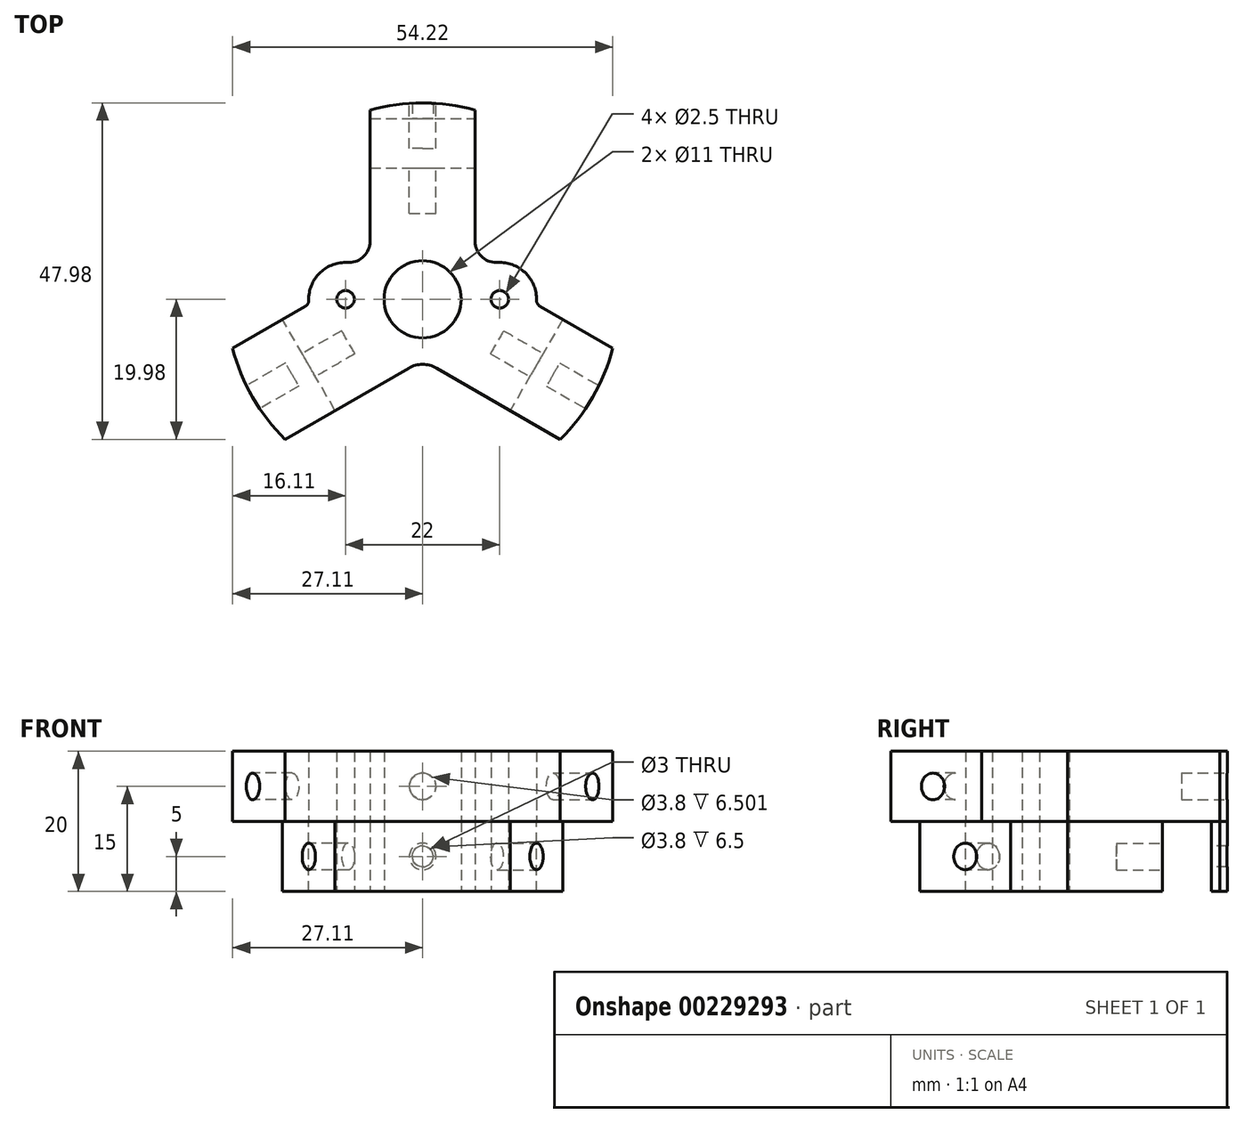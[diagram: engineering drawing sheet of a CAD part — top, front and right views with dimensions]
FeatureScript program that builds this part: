
annotation { "Feature Type Name" : "Feature", "Feature Type Description" : "" }
export const myFeature = defineFeature(function(context is Context, id is Id, definition is map)
    precondition{}
    {
        {
            var Q0;
            Q0=qCreatedBy(makeId("Top.planeOp"),FACE);
            var sketch = newSketch(context, id + "F0", { "sketchPlane" : qUnion([Q0])});
            skArc(sketch, "E0", {"start": v(7.5, 26.98) * mm, "mid": v(0, 28) * mm, "end": v(-7.5, 26.98) * mm});
            skCircle(sketch, "E1", {"center": v(0, 0) * mm, "radius": 5.5 * mm});
            skCircle(sketch, "E2", {"center": v(-11, 0) * mm, "radius": 1.25 * mm});
            skCircle(sketch, "E3", {"center": v(11, 0) * mm, "radius": 1.25 * mm});
            skArc(sketch, "E4", {"start": v(-7.5, 17.18) * mm, "mid": v(-16.24, 9.37) * mm, "end": v(-18.63, -2.1) * mm});
            skCircle(sketch, "E5", {"center": v(0, 0) * mm, "radius": 25.75 * mm, "construction": true});
            skLineSegment(sketch, "E6", {"start": v(12.25, 0) * mm, "end": v(18.75, 0) * mm, "construction": true});
            skLineSegment(sketch, "E7", {"start": v(-7.5, 18.75) * mm, "end": v(7.5, 18.75) * mm});
            skLineSegment(sketch, "E8", {"start": v(-7.5, 18.75) * mm, "end": v(-7.5, 17.18) * mm});
            skLineSegment(sketch, "E9", {"start": v(7.5, 18.75) * mm, "end": v(7.5, 17.18) * mm});
            skLineSegment(sketch, "E10", {"start": v(-7.5, 25.75) * mm, "end": v(7.5, 25.75) * mm});
            skLineSegment(sketch, "E11", {"start": v(-7.5, 25.75) * mm, "end": v(-7.5, 26.98) * mm});
            skLineSegment(sketch, "E12", {"start": v(7.5, 25.75) * mm, "end": v(7.5, 26.98) * mm});
            skLineSegment(sketch, "E13.1.0", {"start": v(-12.49, -15.87) * mm, "end": v(-19.99, -2.88) * mm});
            skLineSegment(sketch, "E13.1.3", {"start": v(-19.99, -2.88) * mm, "end": v(-18.63, -2.1) * mm});
            skLineSegment(sketch, "E13.1.6", {"start": v(-12.49, -15.87) * mm, "end": v(-11.13, -15.09) * mm});
            skLineSegment(sketch, "E13.2.0", {"start": v(19.99, -2.88) * mm, "end": v(12.49, -15.87) * mm});
            skLineSegment(sketch, "E13.2.3", {"start": v(12.49, -15.87) * mm, "end": v(11.13, -15.09) * mm});
            skLineSegment(sketch, "E13.2.6", {"start": v(19.99, -2.88) * mm, "end": v(18.63, -2.1) * mm});
            skArc(sketch, "E14.trimOffspring", {"start": v(-11.13, -15.09) * mm, "mid": v(0, -18.75) * mm, "end": v(11.13, -15.09) * mm});
            skArc(sketch, "E15.trimOffspring", {"start": v(18.63, -2.1) * mm, "mid": v(16.24, 9.37) * mm, "end": v(7.5, 17.18) * mm});
            skSolve(sketch);
        }
        {
            var Q0;
            Q0 = qSketchRegion(id + "F0", true);
            extrude(context, id + "F1", {"entities" : qUnion([Q0]), "depth" : 10 * mm});
        }
        {
            var Q0;
            Q0=makeQuery(id+"F1.opExtrude","SWEPT_FACE",FACE,{"disambiguationData":[OSD([sQuery(id+"F0.wireOp",EDGE,"E13.1.0")])]});
            var sketch = newSketch(context, id + "F2", { "sketchPlane" : qUnion([Q0])});
            skLineSegment(sketch, "E16", {"start": v(0, 10) * mm, "end": v(0, 0) * mm, "construction": true});
            skCircle(sketch, "E17", {"center": v(0, 5) * mm, "radius": 1.9 * mm});
            skSolve(sketch);
        }
        {
            var Q0;
            Q0 = qSketchRegion(id + "F2", true);
            extrude(context, id + "F3", {"entities" : qUnion([Q0]), "oppositeDirection" : true, "depth" : 6.5 * mm});
        }
        {
            var Q0;
            Q0=makeQuery(id+"F3.opExtrude","SWEPT_BODY",BODY,{"disambiguationData":[OSD([sQuery(id+"F2.wireOp",EDGE,"E17")])]});
            var Q1;
            Q1=makeQuery(id+"F1.opExtrude","SWEPT_FACE",FACE,{"disambiguationData":[OSD([sQuery(id+"F0.wireOp",EDGE,"E1")])]});
            circularPattern(context, id + "F4", {"entities" : qUnion([Q0]), "axis" : qUnion([Q1]), "angle" : 360 * degree, "instanceCount" : 3, "equalSpace" : true});
        }
        {
            var Q0;
            Q0=makeQuery(id+"F3.opExtrude","SWEPT_BODY",BODY,{"disambiguationData":[OSD([sQuery(id+"F2.wireOp",EDGE,"E17")])]});
            var Q1;
            Q1=makeQuery(id+"F4.opPattern","COPY",BODY,{"derivedFrom":makeQuery(id+"F3.opExtrude","SWEPT_BODY",BODY,{"disambiguationData":[OSD([sQuery(id+"F2.wireOp",EDGE,"E17")])]}),"instanceName":"1"});
            var Q2;
            Q2=makeQuery(id+"F4.opPattern","COPY",BODY,{"derivedFrom":makeQuery(id+"F3.opExtrude","SWEPT_BODY",BODY,{"disambiguationData":[OSD([sQuery(id+"F2.wireOp",EDGE,"E17")])]}),"instanceName":"2"});
            var Q3;
            Q3=makeQuery(id+"F1.opExtrude","SWEPT_BODY",BODY,{"disambiguationData":[OSD([sQuery(id+"F0.wireOp",EDGE,"E1"),sQuery(id+"F0.wireOp",EDGE,"E2"),sQuery(id+"F0.wireOp",EDGE,"E3"),sQuery(id+"F0.wireOp",EDGE,"E4"),sQuery(id+"F0.wireOp",EDGE,"E7"),sQuery(id+"F0.wireOp",EDGE,"E8"),sQuery(id+"F0.wireOp",EDGE,"E9"),sQuery(id+"F0.wireOp",EDGE,"E13.1.0"),sQuery(id+"F0.wireOp",EDGE,"E13.1.3"),sQuery(id+"F0.wireOp",EDGE,"E13.1.6"),sQuery(id+"F0.wireOp",EDGE,"E13.2.0"),sQuery(id+"F0.wireOp",EDGE,"E13.2.3"),sQuery(id+"F0.wireOp",EDGE,"E13.2.6"),sQuery(id+"F0.wireOp",EDGE,"E14.trimOffspring"),sQuery(id+"F0.wireOp",EDGE,"E15.trimOffspring")])]});
            booleanBodies(context, id + "F5", {"operationType" : BooleanOperationType.SUBTRACTION, "tools" : qUnion([Q0, Q1, Q2]), "targets" : qUnion([Q3])});
        }
        {
            var Q0;
            Q0=makeQuery(id+"F1.opExtrude","SWEPT_FACE",FACE,{"disambiguationData":[OSD([sQuery(id+"F0.wireOp",EDGE,"E10")])]});
            var sketch = newSketch(context, id + "F6", { "sketchPlane" : qUnion([Q0])});
            skLineSegment(sketch, "E18", {"start": v(0, 10) * mm, "end": v(0, 0) * mm, "construction": true});
            skCircle(sketch, "E19", {"center": v(0, 5) * mm, "radius": 1.5 * mm});
            skSolve(sketch);
        }
        {
            var Q0;
            Q0 = qSketchRegion(id + "F6", true);
            var Q1;
            Q1=sQuery(id+"F6.wireOp",EDGE,"E19");
            extrude(context, id + "F7", {"entities" : qUnion([Q0]), "operationType" : NewBodyOperationType.REMOVE, "surfaceEntities" : qUnion([Q1]), "endBound" : BoundingType.UP_TO_NEXT, "oppositeDirection" : true, "depth" : 25 * mm});
        }
        {
            var Q0;
            Q0=makeQuery(id+"F1.opExtrude","CAP_FACE",FACE,{"disambiguationData":[OSD([sQuery(id+"F0.wireOp",EDGE,"E1"),sQuery(id+"F0.wireOp",EDGE,"E2"),sQuery(id+"F0.wireOp",EDGE,"E3"),sQuery(id+"F0.wireOp",EDGE,"E4"),sQuery(id+"F0.wireOp",EDGE,"E7"),sQuery(id+"F0.wireOp",EDGE,"E8"),sQuery(id+"F0.wireOp",EDGE,"E9"),sQuery(id+"F0.wireOp",EDGE,"E13.1.0"),sQuery(id+"F0.wireOp",EDGE,"E13.1.3"),sQuery(id+"F0.wireOp",EDGE,"E13.1.6"),sQuery(id+"F0.wireOp",EDGE,"E13.2.0"),sQuery(id+"F0.wireOp",EDGE,"E13.2.3"),sQuery(id+"F0.wireOp",EDGE,"E13.2.6"),sQuery(id+"F0.wireOp",EDGE,"E14.trimOffspring"),sQuery(id+"F0.wireOp",EDGE,"E15.trimOffspring")])],"isStart":false});
            var sketch = newSketch(context, id + "F8", { "sketchPlane" : qUnion([Q0])});
            skArc(sketch, "E20", {"start": v(-11, 5.25) * mm, "mid": v(-14.75, 3.67) * mm, "end": v(-16.25, -0.12) * mm});
            skArc(sketch, "E21", {"start": v(16.25, -0.12) * mm, "mid": v(14.75, 3.67) * mm, "end": v(11, 5.25) * mm});
            skLineSegment(sketch, "E22", {"start": v(-11, 5.25) * mm, "end": v(-10.5, 5.25) * mm});
            skLineSegment(sketch, "E23", {"start": v(-7.5, 17.18) * mm, "end": v(-7.5, 8.25) * mm});
            skLineSegment(sketch, "E24", {"start": v(7.5, 17.18) * mm, "end": v(7.5, 8.25) * mm});
            skLineSegment(sketch, "E25", {"start": v(-18.63, -2.1) * mm, "end": v(-16.75, -1) * mm});
            skLineSegment(sketch, "E26", {"start": v(18.63, -2.1) * mm, "end": v(16.75, -1) * mm});
            skLineSegment(sketch, "E27.trimOffspring", {"start": v(10.5, 5.25) * mm, "end": v(11, 5.25) * mm});
            skPoint(sketch, "E28.visualSharp", {"position": v(-7.5, 5.25) * mm});
            skArc(sketch, "E28.filletArc", {"start": v(-10.5, 5.25) * mm, "mid": v(-8.38, 6.13) * mm, "end": v(-7.5, 8.25) * mm});
            skPoint(sketch, "E29.visualSharp", {"position": v(7.5, 5.25) * mm});
            skArc(sketch, "E29.filletArc", {"start": v(7.5, 8.25) * mm, "mid": v(8.38, 6.13) * mm, "end": v(10.5, 5.25) * mm});
            skPoint(sketch, "E30.visualSharp", {"position": v(-16.2, -0.7) * mm});
            skArc(sketch, "E30.filletArc", {"start": v(-16.75, -1) * mm, "mid": v(-16.38, -0.63) * mm, "end": v(-16.25, -0.12) * mm});
            skPoint(sketch, "E31.visualSharp", {"position": v(16.2, -0.7) * mm});
            skArc(sketch, "E31.filletArc", {"start": v(16.25, -0.12) * mm, "mid": v(16.38, -0.63) * mm, "end": v(16.75, -1) * mm});
            skArc(sketch, "E32", {"start": v(18.63, -2.1) * mm, "mid": v(16.24, 9.38) * mm, "end": v(7.5, 17.18) * mm});
            skArc(sketch, "E33", {"start": v(-7.5, 17.18) * mm, "mid": v(-16.24, 9.37) * mm, "end": v(-18.63, -2.1) * mm});
            skLineSegment(sketch, "E34", {"start": v(-11.13, -15.09) * mm, "end": v(-2, -9.81) * mm});
            skLineSegment(sketch, "E35", {"start": v(2, -9.81) * mm, "end": v(11.13, -15.09) * mm});
            skPoint(sketch, "E36.visualSharp", {"position": v(0, -8.66) * mm});
            skArc(sketch, "E36.filletArc", {"start": v(2, -9.81) * mm, "mid": v(0, -9.28) * mm, "end": v(-2, -9.81) * mm});
            skArc(sketch, "E37", {"start": v(-11.13, -15.09) * mm, "mid": v(0, -18.75) * mm, "end": v(11.13, -15.09) * mm});
            skSolve(sketch);
        }
        {
            var Q0;
            Q0 = qSketchRegion(id + "F8", true);
            extrude(context, id + "F9", {"entities" : qUnion([Q0]), "operationType" : NewBodyOperationType.REMOVE, "endBound" : BoundingType.UP_TO_NEXT, "oppositeDirection" : true, "depth" : 25 * mm});
        }
        {
            var Q0;
            Q0=makeQuery(id+"F1.opExtrude","CAP_FACE",FACE,{"disambiguationData":[OSD([sQuery(id+"F0.wireOp",EDGE,"E1"),sQuery(id+"F0.wireOp",EDGE,"E2"),sQuery(id+"F0.wireOp",EDGE,"E3"),sQuery(id+"F0.wireOp",EDGE,"E4"),sQuery(id+"F0.wireOp",EDGE,"E7"),sQuery(id+"F0.wireOp",EDGE,"E8"),sQuery(id+"F0.wireOp",EDGE,"E9"),sQuery(id+"F0.wireOp",EDGE,"E13.1.0"),sQuery(id+"F0.wireOp",EDGE,"E13.1.3"),sQuery(id+"F0.wireOp",EDGE,"E13.1.6"),sQuery(id+"F0.wireOp",EDGE,"E13.2.0"),sQuery(id+"F0.wireOp",EDGE,"E13.2.3"),sQuery(id+"F0.wireOp",EDGE,"E13.2.6"),sQuery(id+"F0.wireOp",EDGE,"E14.trimOffspring"),sQuery(id+"F0.wireOp",EDGE,"E15.trimOffspring")])],"isStart":false});
            var sketch = newSketch(context, id + "F10", { "sketchPlane" : qUnion([Q0])});
            skArc(sketch, "E38", {"start": v(-27.11, -7) * mm, "mid": v(-24.25, -14) * mm, "end": v(-19.61, -19.98) * mm});
            skCircle(sketch, "E39", {"center": v(0, 0) * mm, "radius": 5.5 * mm});
            skCircle(sketch, "E40", {"center": v(-11, 0) * mm, "radius": 1.25 * mm});
            skCircle(sketch, "E41", {"center": v(11, 0) * mm, "radius": 1.25 * mm});
            skArc(sketch, "E42", {"start": v(-11, 5.25) * mm, "mid": v(-14.75, 3.67) * mm, "end": v(-16.25, -0.12) * mm});
            skArc(sketch, "E43", {"start": v(16.25, -0.12) * mm, "mid": v(14.75, 3.67) * mm, "end": v(11, 5.25) * mm});
            skLineSegment(sketch, "E44", {"start": v(-11, 5.25) * mm, "end": v(-10.5, 5.25) * mm});
            skLineSegment(sketch, "E45", {"start": v(-7.5, 26.98) * mm, "end": v(-7.5, 8.25) * mm});
            skLineSegment(sketch, "E46", {"start": v(7.5, 26.98) * mm, "end": v(7.5, 8.25) * mm});
            skLineSegment(sketch, "E47", {"start": v(27.11, -7) * mm, "end": v(16.75, -1) * mm});
            skLineSegment(sketch, "E48", {"start": v(19.61, -19.98) * mm, "end": v(2, -9.81) * mm});
            skLineSegment(sketch, "E49", {"start": v(-2, -9.81) * mm, "end": v(-19.61, -19.98) * mm});
            skLineSegment(sketch, "E50", {"start": v(-27.11, -7) * mm, "end": v(-16.75, -1) * mm});
            skArc(sketch, "E51.trimOffspring", {"start": v(7.5, 26.98) * mm, "mid": v(0, 28) * mm, "end": v(-7.5, 26.98) * mm});
            skArc(sketch, "E52.trimOffspring", {"start": v(19.61, -19.98) * mm, "mid": v(24.25, -14) * mm, "end": v(27.11, -7) * mm});
            skLineSegment(sketch, "E53.trimOffspring", {"start": v(10.5, 5.25) * mm, "end": v(11, 5.25) * mm});
            skPoint(sketch, "E54.visualSharp", {"position": v(0, -8.66) * mm});
            skArc(sketch, "E54.filletArc", {"start": v(2, -9.81) * mm, "mid": v(0, -9.28) * mm, "end": v(-2, -9.81) * mm});
            skPoint(sketch, "E55.visualSharp", {"position": v(-7.5, 5.25) * mm});
            skArc(sketch, "E55.filletArc", {"start": v(-10.5, 5.25) * mm, "mid": v(-8.38, 6.13) * mm, "end": v(-7.5, 8.25) * mm});
            skPoint(sketch, "E56.visualSharp", {"position": v(7.5, 5.25) * mm});
            skArc(sketch, "E56.filletArc", {"start": v(7.5, 8.25) * mm, "mid": v(8.38, 6.13) * mm, "end": v(10.5, 5.25) * mm});
            skPoint(sketch, "E57.visualSharp", {"position": v(16.2, -0.7) * mm});
            skArc(sketch, "E57.filletArc", {"start": v(16.25, -0.12) * mm, "mid": v(16.38, -0.63) * mm, "end": v(16.75, -1) * mm});
            skPoint(sketch, "E58.visualSharp", {"position": v(-16.2, -0.7) * mm});
            skArc(sketch, "E58.filletArc", {"start": v(-16.75, -1) * mm, "mid": v(-16.38, -0.63) * mm, "end": v(-16.25, -0.12) * mm});
            skSolve(sketch);
        }
        {
            var Q0;
            Q0 = qSketchRegion(id + "F10", true);
            extrude(context, id + "F11", {"entities" : qUnion([Q0]), "depth" : 10 * mm});
        }
        {
            var Q0;
            Q0=makeQuery(id+"F11.opExtrude","CAP_EDGE",EDGE,{"disambiguationData":[OSD([sQuery(id+"F10.wireOp",EDGE,"E51.trimOffspring")])],"isStart":false});
            cPoint(context, id + "F12", {"entities" : qUnion([Q0]), "parameter" : 0.5});
        }
        {
            var Q0;
            Q0=qCreatedBy(makeId("Front.planeOp"),FACE);
            var Q1;
            Q1 = qCreatedBy(id + "F12" ,VERTEX);
            cPlane(context, id + "F13", {"entities" : qUnion([Q0, Q1]), "cplaneType" : CPlaneType.PLANE_POINT, "offset" : 25 * mm, "width" : 150 * mm, "height" : 150 * mm});
        }
        {
            var Q0;
            Q0=qCreatedBy(id+"F13.planeOp",FACE);
            var sketch = newSketch(context, id + "F14", { "sketchPlane" : qUnion([Q0])});
            skLineSegment(sketch, "E59", {"start": v(0, 20) * mm, "end": v(0, 10) * mm, "construction": true});
            skCircle(sketch, "E60", {"center": v(0, 15) * mm, "radius": 1.9 * mm});
            skSolve(sketch);
        }
        {
            var Q0;
            Q0 = qSketchRegion(id + "F14", true);
            extrude(context, id + "F15", {"entities" : qUnion([Q0]), "endBound" : BoundingType.SYMMETRIC, "depth" : 6.5 * mm * 2});
        }
        {
            var Q0;
            Q0=makeQuery(id+"F15.opExtrude","SWEPT_BODY",BODY,{"disambiguationData":[OSD([sQuery(id+"F14.wireOp",EDGE,"E60")])]});
            var Q1;
            Q1=makeQuery(id+"F11.opExtrude","SWEPT_FACE",FACE,{"disambiguationData":[OSD([sQuery(id+"F10.wireOp",EDGE,"E39")])]});
            circularPattern(context, id + "F16", {"operationType" : NewBodyOperationType.REMOVE, "entities" : qUnion([Q0]), "axis" : qUnion([Q1]), "angle" : 360 * degree, "instanceCount" : 3, "equalSpace" : true});
        }
    });
